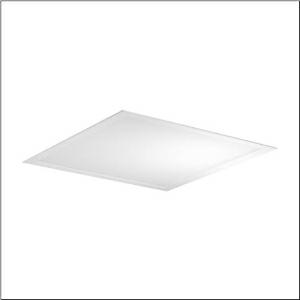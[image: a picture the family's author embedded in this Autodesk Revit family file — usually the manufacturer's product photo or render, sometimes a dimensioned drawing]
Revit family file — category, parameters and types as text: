
# Revit family: apollon_21_square_51mq11wd2414
name_source: partatom
category: Lighting Fixtures
units: mm (PartAtom-declared; Revit-internal decimal feet)

## family parameters
Cut with Voids When Loaded = No
Host = Face
Light Source = No
Part Type = Normal
Room Calculation Point = No
Round Connector Dimension = Use Diameter
Shared = No

## types (1)
- Apollon 21 square (1 x LED, 4200 lm, 24.7 W, 4000K)
    Apparent Load = 25 VA
    CIE Flux Codes = 60 87 97 100 100
    Color Rendering = 80
    Color Temperature = 4000K
    Default Elevation = 1800 mm
    Description = Apollon 21 square, office luminaire, primary optical cover: micro prismatic cover, of PMMA, CAT 2 (L<= 3000cd/m²), light emission: direct distribution, primary light characteristic: symmetric, installation type: lay-in mounting, LED, rated luminous flux: 4.200lm, luminous efficacy: 170lm/W, light colour: 840, colour temperature: 4000K, control gear: DALI 2, Multilumen, with terminal, 5-pole, mains connection: 220..240V, AC/DC, 0/50..60Hz, rated input power: 24.7W, suitable for self-contained emergency lighting element 59MQE002602A with integrated self-test function according to EN 60598-2-22, housing, of aluminium, coated, traffic white (RAL 9016), module: M625, length: 620mm, width: 620mm, height: 55mm, recess depth: 180mm, housing upper side, of sheet steel, galvanised, protection rating (complete): IP20, protection rating (lamp compartment, on room side): IP50, insulation class (complete): insulation class II (safety insulation), certification: CE, ENEC, impact resistance: IK03, permissible operating ambient temperature: -20..+45°C, permissible storage temperature: -40..+80°C, standard: EN 60598-2-22, packaging unit: 1 piece
    Height = 0 mm  [stored 0 ft]
    Lamp = 1 x LED
    Lamp Light Flux = 4200 lm
    Lamp Power = 24.7 W
    Lamp count = 1
    Length = 620 mm
    Luminous efficacy = 170 lm/W
    Manufacturer = Siteco
    ModVariant = No
    Model = 51MQ11WD2414
    Mounting Place = Ceiling
    Mounting Type = Recessed
    Number of Poles = 1
    OnlyDefault = Yes
    Power Factor = 1
    Product Name = Apollon 21 square
    Product group = office luminaire | ceiling recessed
    ProductGroupID = 400
    Protection Class = Protection class II
    Protection Degree = IP 20
    RLX_Detail_Level = 1
    RLX_Emergency_Light_Flux = 0 lm
    RLX_Emergency_Type = 0
    RLX_Emergency_Type_DB = No
    RlxData = <blob elided: 13169 chars, md5=bf9fefe5>
    Socket = socket
    Standby Power = 0 W
    System Light Flux = 4200 lm
    System Power = 25 W
    Type Comments = Product without accessories
    Type Image = l_1291054.jpg
    URL = http://relux.com
    VarID = ---
    Voltage = 0 V
    Weight = 0.00 kg
    Width = 620 mm

note: [stored X ft] marks values corroborated as IEEE doubles in the binary element streams (Revit-internal decimal feet)

## geometry (parser evidence)
native form markers: Sweep x11
no freeform markers — native parametric forms only
